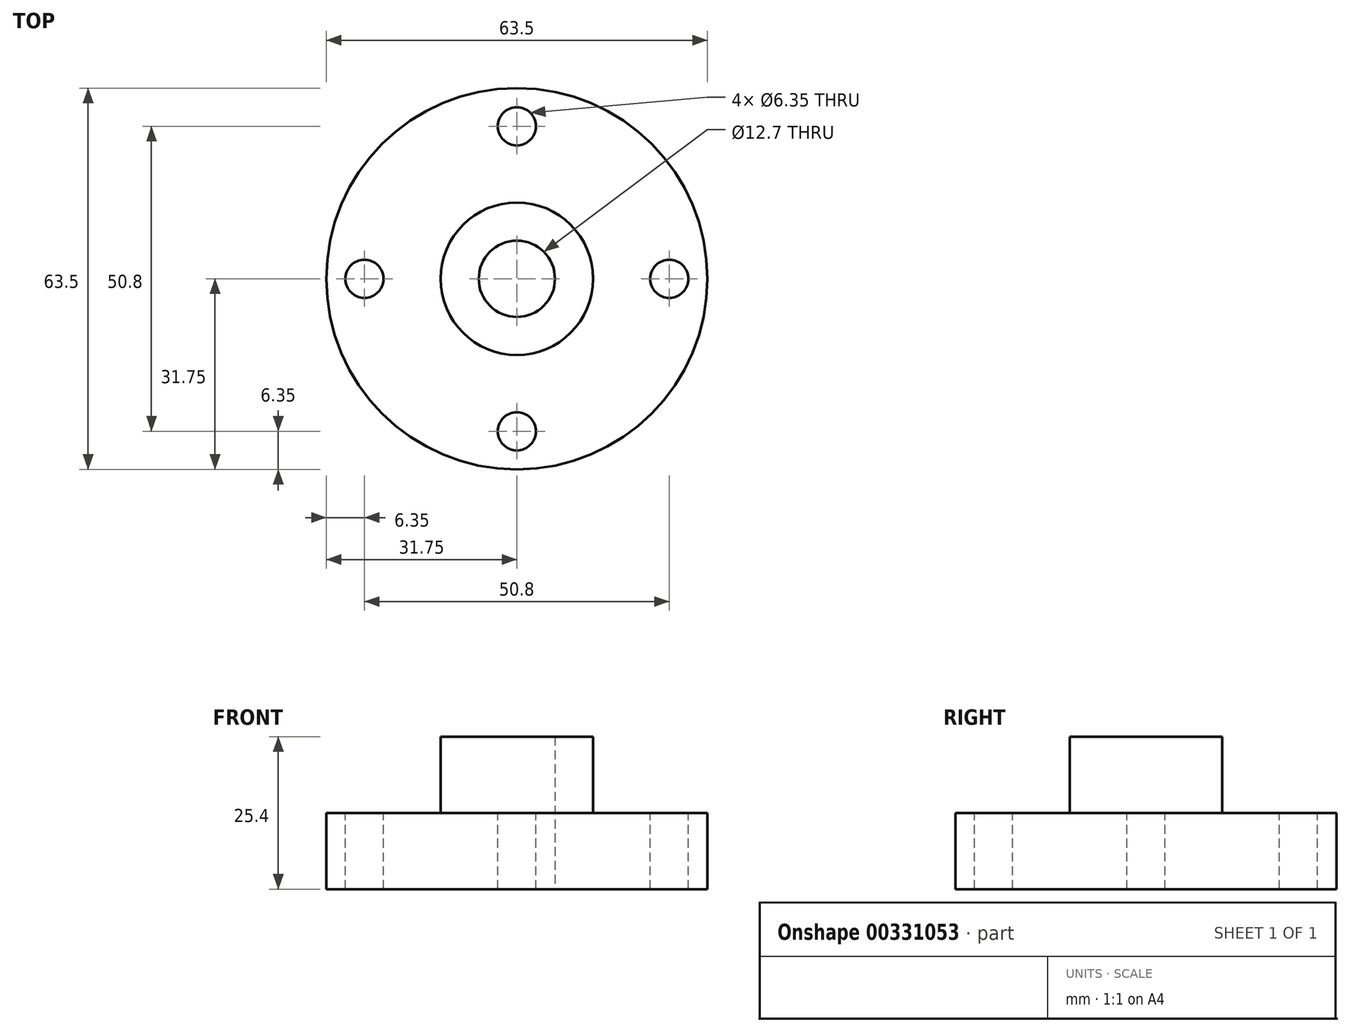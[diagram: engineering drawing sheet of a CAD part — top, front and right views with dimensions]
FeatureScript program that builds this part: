
annotation { "Feature Type Name" : "Feature", "Feature Type Description" : "" }
export const myFeature = defineFeature(function(context is Context, id is Id, definition is map)
    precondition{}
    {
        {
            var Q0;
            Q0=qCreatedBy(makeId("Top.planeOp"),FACE);
            var sketch = newSketch(context, id + "F0", { "sketchPlane" : qUnion([Q0])});
            skCircle(sketch, "E0", {"center": v(0, 0) * mm, "radius": 31.75 * mm});
            skCircle(sketch, "E1", {"center": v(0, 0) * mm, "radius": 12.7 * mm});
            skCircle(sketch, "E2", {"center": v(0, 0) * mm, "radius": 6.35 * mm});
            skSolve(sketch);
        }
        {
            var Q0;
            Q0=makeQuery(id+"F0.imprint","IMPRINT",FACE,{"disambiguationData":[TD([[makeQuery(id+"F0.imprint","IMPRINT",EDGE,{"derivedFrom":sQuery(id+"F0.wireOp",EDGE,"E0")}),1.0]])]});
            extrude(context, id + "F1", {"entities" : qUnion([Q0]), "depth" : 12.7 * mm});
        }
        {
            var Q0;
            Q0=makeQuery(id+"F0.imprint","IMPRINT",FACE,{"disambiguationData":[TD([[makeQuery(id+"F0.imprint","IMPRINT",EDGE,{"derivedFrom":sQuery(id+"F0.wireOp",EDGE,"E1")}),1.0]])]});
            extrude(context, id + "F2", {"entities" : qUnion([Q0]), "operationType" : NewBodyOperationType.ADD, "depth" : 25.4 * mm});
        }
        {
            var Q0;
            Q0=makeQuery(id+"F1.opExtrude","CAP_FACE",FACE,{"disambiguationData":[OSD([sQuery(id+"F0.wireOp",EDGE,"E0"),sQuery(id+"F0.wireOp",EDGE,"E1")])],"isStart":false});
            var sketch = newSketch(context, id + "F3", { "sketchPlane" : qUnion([Q0])});
            skPoint(sketch, "E3", {"position": v(0, 25.4) * mm});
            skPoint(sketch, "E4.1.0", {"position": v(-25.4, 0) * mm});
            skPoint(sketch, "E4.2.0", {"position": v(0, -25.4) * mm});
            skPoint(sketch, "E4.3.0", {"position": v(25.4, 0) * mm});
            skPoint(sketch, "E4.center", {"position": v(0, 0) * mm});
            skSolve(sketch);
        }
        {
            var Q0;
            Q0=sQuery(id+"F3.wireOp",VERTEX,"E3");
            var Q1;
            Q1=sQuery(id+"F3.wireOp",VERTEX,"E4.3.0");
            var Q2;
            Q2=sQuery(id+"F3.wireOp",VERTEX,"E4.2.0");
            var Q3;
            Q3=sQuery(id+"F3.wireOp",VERTEX,"E4.1.0");
            var Q4;
            Q4=makeQuery(id+"F1.opExtrude","SWEPT_BODY",BODY,{"disambiguationData":[OSD([sQuery(id+"F0.wireOp",EDGE,"E0"),sQuery(id+"F0.wireOp",EDGE,"E1")])]});
            hole(context, id + "F4", {"style" : HoleStyle.SIMPLE, "endStyle" : HoleEndStyle.THROUGH, "holeDiameter" : 6.35 * mm, "tappedDepth" : 12.7 * mm, "tapClearance" : 3, "locations" : qUnion([Q0, Q1, Q2, Q3]), "scope" : qUnion([Q4])});
        }
    });
